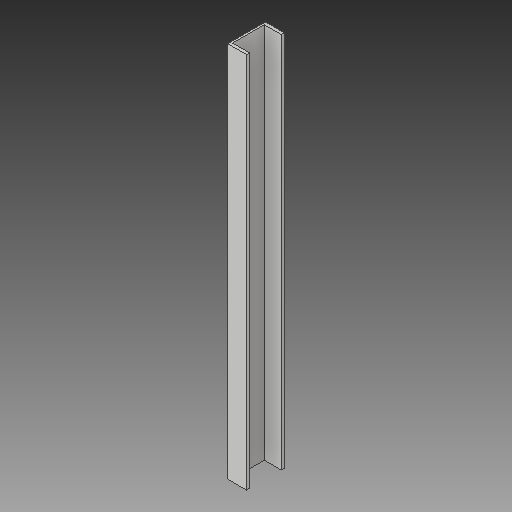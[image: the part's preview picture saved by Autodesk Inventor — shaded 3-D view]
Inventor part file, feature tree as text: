
AUTODESK INVENTOR PART (.ipt)
format: ipt  version: 2019 (Build 230136000, 136)  size: 86,528 bytes
history: native  units: in
note: dims shown in document units (in); Inventor stores cm internally (conversion verified against a paired STEP export)
features: other x3, sketch x1
ambient origin geometry x8: Origin, YZ Plane, XZ Plane, XY Plane, X Axis, Y Axis, Z Axis, Center Point
bodies: Solid1 (feature_tree)
feature tree (4):
  other  "Channel1_MIR_MIR2.ipt"
  other  "Solid1::Channel1_MIR_MIR2.ipt"
  other  "TaggingFeature1"
  sketch  "Sketch1"  dims[d0=0.3937in]
